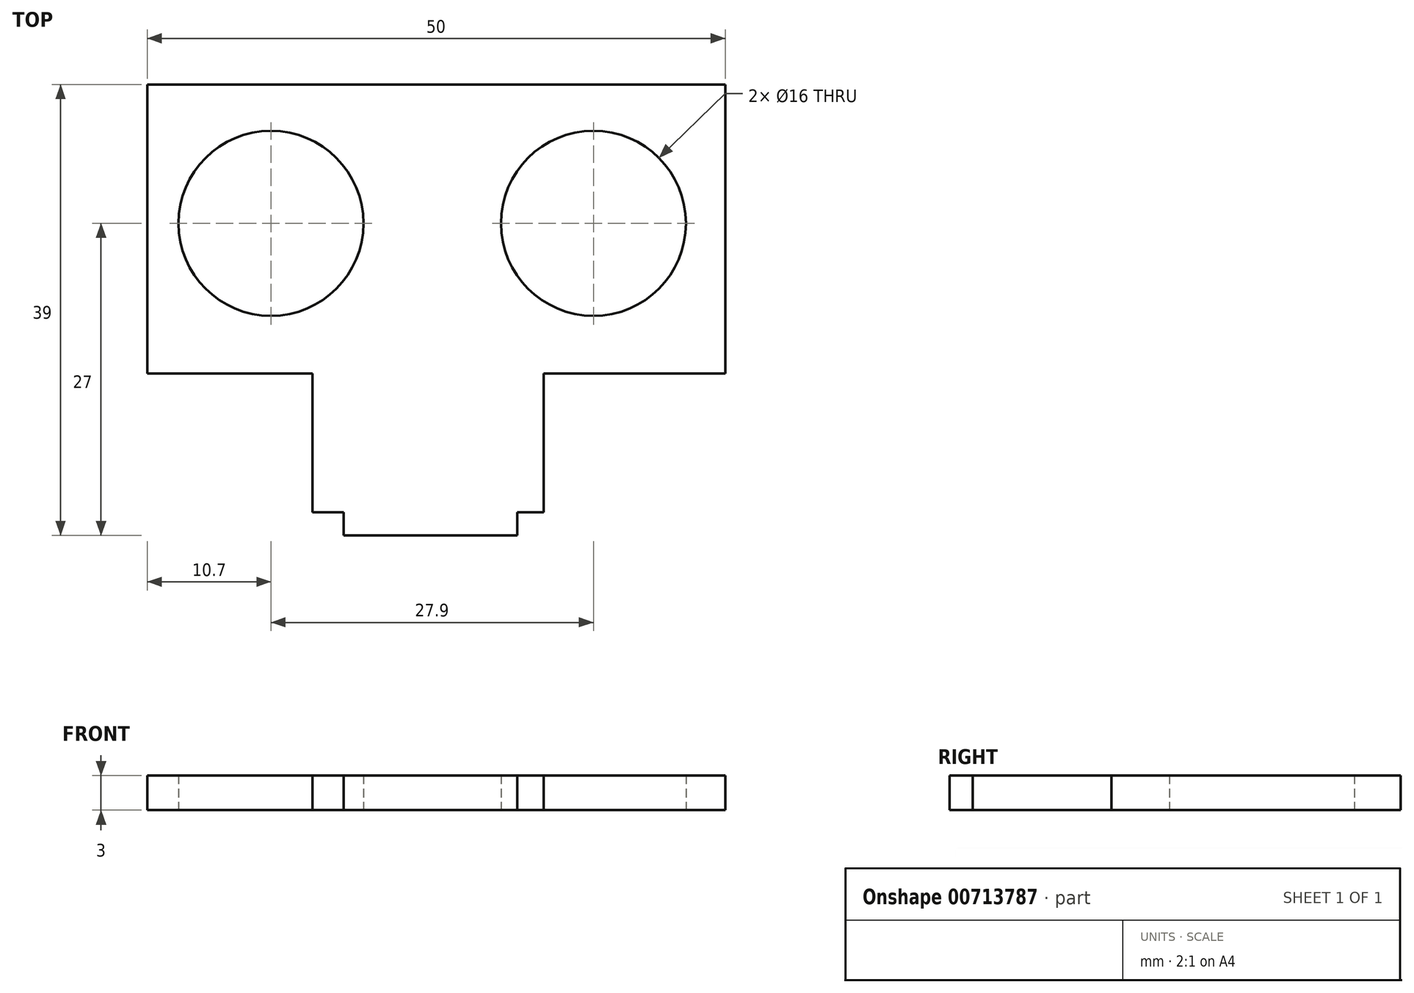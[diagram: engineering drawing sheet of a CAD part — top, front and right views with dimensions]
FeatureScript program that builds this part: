
annotation { "Feature Type Name" : "Feature", "Feature Type Description" : "" }
export const myFeature = defineFeature(function(context is Context, id is Id, definition is map)
    precondition{}
    {
        {
            var Q0;
            Q0=qCreatedBy(makeId("Top.planeOp"),FACE);
            var sketch = newSketch(context, id + "F0", { "sketchPlane" : qUnion([Q0])});
            skLineSegment(sketch, "E0.bottom", {"start": v(-24.05, 51) * mm, "end": v(25.95, 51) * mm});
            skLineSegment(sketch, "E0.top", {"start": v(-24.05, 26) * mm, "end": v(25.95, 26) * mm});
            skLineSegment(sketch, "E0.left", {"start": v(-24.05, 51) * mm, "end": v(-24.05, 26) * mm});
            skLineSegment(sketch, "E0.right", {"start": v(25.95, 51) * mm, "end": v(25.95, 26) * mm});
            skCircle(sketch, "E1", {"center": v(-13.35, 39) * mm, "radius": 8 * mm});
            skCircle(sketch, "E2", {"center": v(14.55, 39) * mm, "radius": 8 * mm});
            skLineSegment(sketch, "E3.bottom", {"start": v(-9.75, 26) * mm, "end": v(10.25, 26) * mm});
            skLineSegment(sketch, "E3.top", {"start": v(-9.75, 14) * mm, "end": v(10.25, 14) * mm});
            skLineSegment(sketch, "E3.left", {"start": v(-9.75, 26) * mm, "end": v(-9.75, 14) * mm});
            skLineSegment(sketch, "E3.right", {"start": v(10.25, 26) * mm, "end": v(10.25, 14) * mm});
            skLineSegment(sketch, "E4.bottom", {"start": v(-7.05, 14) * mm, "end": v(7.95, 14) * mm});
            skLineSegment(sketch, "E4.top", {"start": v(-7.05, 12) * mm, "end": v(7.95, 12) * mm});
            skLineSegment(sketch, "E4.left", {"start": v(-7.05, 14) * mm, "end": v(-7.05, 12) * mm});
            skLineSegment(sketch, "E4.right", {"start": v(7.95, 14) * mm, "end": v(7.95, 12) * mm});
            skSolve(sketch);
        }
        {
            var Q0;
            Q0=qSketchRegion(id+"F0",true);
            extrude(context, id + "F1", {"entities" : qUnion([Q0]), "depth" : 3 * mm, "offsetDistance" : 25 * mm});
        }
    });
